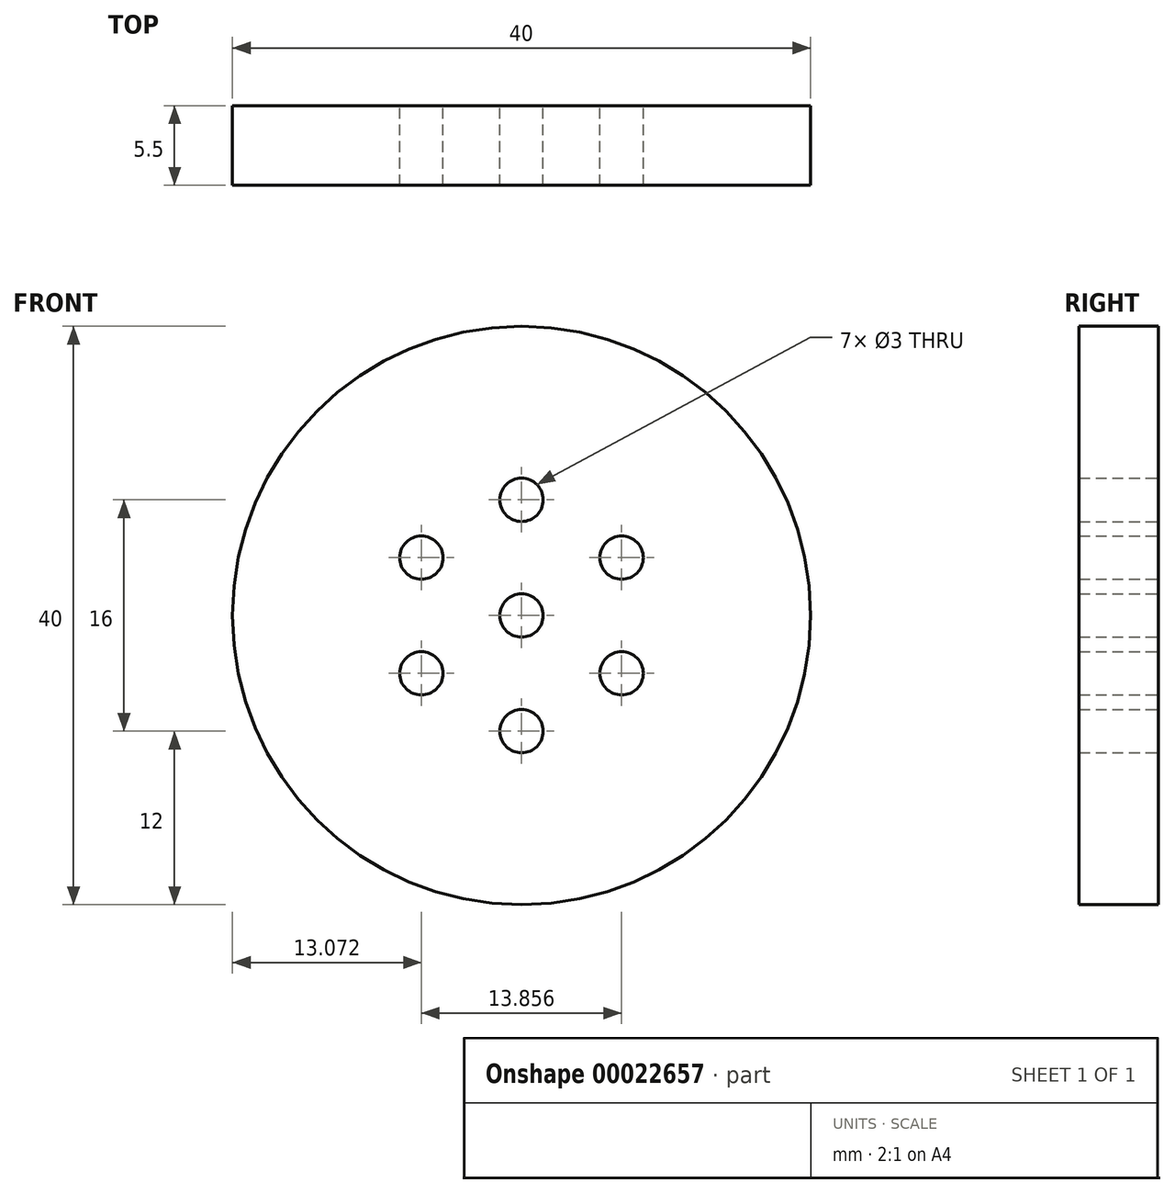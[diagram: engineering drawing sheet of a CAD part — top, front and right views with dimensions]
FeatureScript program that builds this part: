
annotation { "Feature Type Name" : "Feature", "Feature Type Description" : "" }
export const myFeature = defineFeature(function(context is Context, id is Id, definition is map)
    precondition{}
    {
        {
            var Q0;
            Q0=qCreatedBy(makeId("Front.planeOp"),FACE);
            var sketch = newSketch(context, id + "F0", { "sketchPlane" : qUnion([Q0])});
            skCircle(sketch, "E0", {"center": v(0, 0) * mm, "radius": 1.5 * mm});
            skCircle(sketch, "E1", {"center": v(0, 0) * mm, "radius": 4 * mm});
            skCircle(sketch, "E2", {"center": v(0, 0) * mm, "radius": 17 * mm});
            skCircle(sketch, "E3", {"center": v(0, 0) * mm, "radius": 20 * mm});
            skCircle(sketch, "E4", {"center": v(0, -8) * mm, "radius": 1.5 * mm});
            skCircle(sketch, "E5.1.0", {"center": v(6.93, -4) * mm, "radius": 1.5 * mm});
            skCircle(sketch, "E5.2.0", {"center": v(6.93, 4) * mm, "radius": 1.5 * mm});
            skCircle(sketch, "E5.3.0", {"center": v(0, 8) * mm, "radius": 1.5 * mm});
            skCircle(sketch, "E5.4.0", {"center": v(-6.93, 4) * mm, "radius": 1.5 * mm});
            skCircle(sketch, "E5.5.0", {"center": v(-6.93, -4) * mm, "radius": 1.5 * mm});
            skSolve(sketch);
        }
        {
            var Q0;
            Q0=makeQuery(id+"F0.imprint","IMPRINT",FACE,{"disambiguationData":[TD([[makeQuery(id+"F0.imprint","IMPRINT",EDGE,{"derivedFrom":sQuery(id+"F0.wireOp",EDGE,"E2")}),-1.0]])]});
            var Q1;
            Q1=makeQuery(id+"F0.imprint","IMPRINT",FACE,{"disambiguationData":[TD([[makeQuery(id+"F0.imprint","IMPRINT",EDGE,{"derivedFrom":sQuery(id+"F0.wireOp",EDGE,"E0")}),-1.0]])]});
            var Q2;
            Q2=makeQuery(id+"F0.imprint","IMPRINT",FACE,{"disambiguationData":[TD([[makeQuery(id+"F0.imprint","IMPRINT",EDGE,{"derivedFrom":sQuery(id+"F0.wireOp",EDGE,"E1")}),-1.0]])]});
            extrude(context, id + "F1", {"entities" : qUnion([Q0, Q1, Q2]), "endBound" : BoundingType.SYMMETRIC, "depth" : 5.5 * mm});
        }
    });
